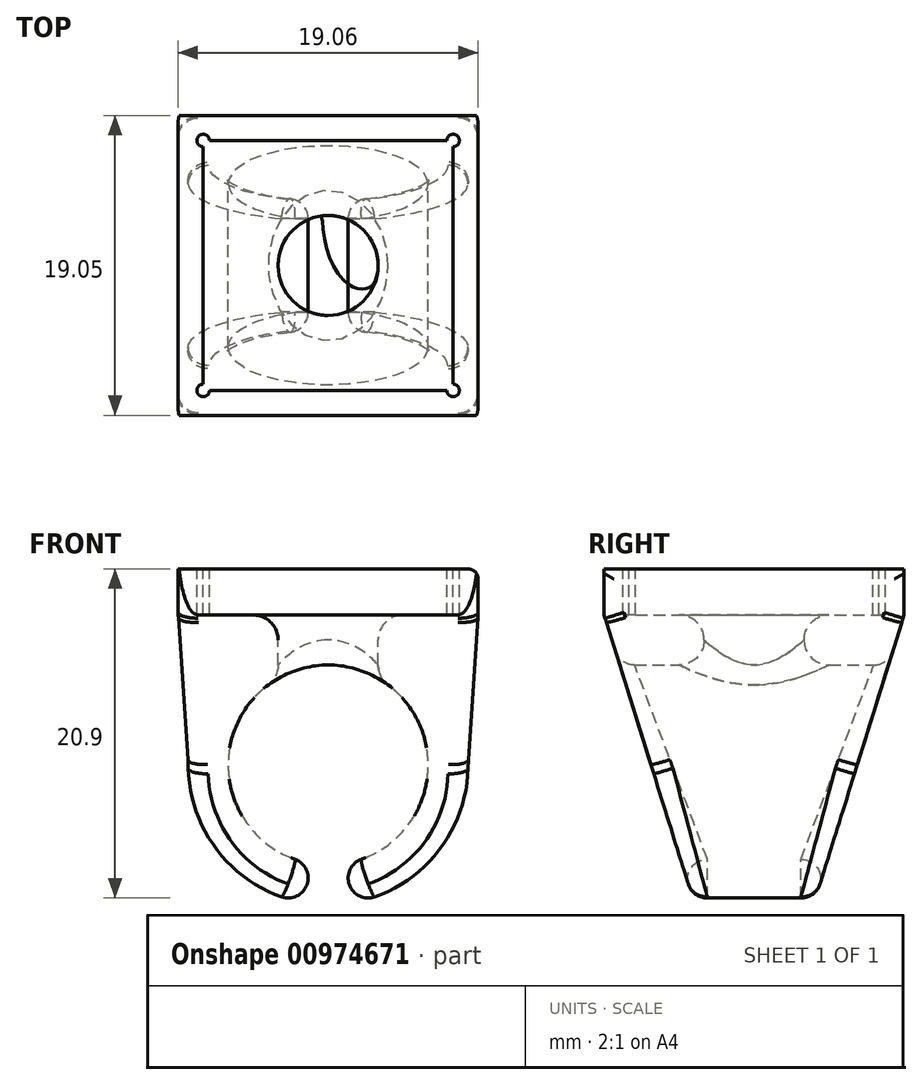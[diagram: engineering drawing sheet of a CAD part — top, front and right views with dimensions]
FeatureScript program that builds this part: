
annotation { "Feature Type Name" : "Feature", "Feature Type Description" : "" }
export const myFeature = defineFeature(function(context is Context, id is Id, definition is map)
    precondition{}
    {
        {
            var Q0;
            Q0=qCreatedBy(makeId("Front.planeOp"),FACE);
            var sketch = newSketch(context, id + "F0", { "sketchPlane" : qUnion([Q0])});
            skCircle(sketch, "E0", {"center": v(0, 0) * mm, "radius": 6.35 * mm});
            skCircle(sketch, "E1", {"center": v(0, 0) * mm, "radius": 8.9 * mm});
            skLineSegment(sketch, "E2", {"start": v(-8.9, 0) * mm, "end": v(-9.53, 9.52) * mm});
            skLineSegment(sketch, "E3", {"start": v(-9.53, 9.52) * mm, "end": v(-9.53, 12.45) * mm});
            skLineSegment(sketch, "E4", {"start": v(-9.53, 12.45) * mm, "end": v(-7.94, 12.45) * mm});
            skLineSegment(sketch, "E5", {"start": v(-7.94, 12.45) * mm, "end": v(-7.94, 9.52) * mm});
            skLineSegment(sketch, "E6", {"start": v(-7.94, 9.52) * mm, "end": v(0, 9.53) * mm});
            skLineSegment(sketch, "E7", {"start": v(0, 9.52) * mm, "end": v(0, 0) * mm});
            skLineSegment(sketch, "E8.MirrorCS", {"start": v(7.94, 9.52) * mm, "end": v(0, 9.53) * mm});
            skLineSegment(sketch, "E9.MirrorCS", {"start": v(7.94, 12.45) * mm, "end": v(7.94, 9.53) * mm});
            skLineSegment(sketch, "E10.MirrorCS", {"start": v(9.52, 12.45) * mm, "end": v(7.94, 12.45) * mm});
            skLineSegment(sketch, "E11.MirrorCS", {"start": v(9.53, 9.53) * mm, "end": v(9.53, 12.45) * mm});
            skLineSegment(sketch, "E12.MirrorCS", {"start": v(8.9, 0) * mm, "end": v(9.53, 9.52) * mm});
            skLineSegment(sketch, "E13", {"start": v(0, 0) * mm, "end": v(-1.27, 0) * mm});
            skLineSegment(sketch, "E14", {"start": v(-1.27, 0) * mm, "end": v(-1.27, -9.53) * mm});
            skLineSegment(sketch, "E15", {"start": v(-1.27, -9.53) * mm, "end": v(0, -9.53) * mm});
            skLineSegment(sketch, "E16.MirrorCS", {"start": v(0, 0) * mm, "end": v(1.27, 0) * mm});
            skLineSegment(sketch, "E17.MirrorCS", {"start": v(1.27, 0) * mm, "end": v(1.27, -9.53) * mm});
            skLineSegment(sketch, "E18.MirrorCS", {"start": v(1.27, -9.53) * mm, "end": v(0, -9.53) * mm});
            skSolve(sketch);
        }
        {
            var Q0;
            {var subQ0=sQuery(id+"F0.wireOp",EDGE,"E2");Q0=makeQuery(id+"F0.imprint","IMPRINT",FACE,{"disambiguationData":[TD([[makeQuery(id+"F0.imprint","IMPRINT",EDGE,{"derivedFrom":subQ0}),-1.0]])]});}
            var Q1;
            {var subQ0=sQuery(id+"F0.wireOp",EDGE,"E8.MirrorCS");Q1=makeQuery(id+"F0.imprint","IMPRINT",FACE,{"disambiguationData":[TD([[makeQuery(id+"F0.imprint","IMPRINT",EDGE,{"derivedFrom":subQ0}),1.0]])]});}
            var Q2;
            {var subQ1=sQuery(id+"F0.wireOp",EDGE,"E0");var subQ6=sQuery(id+"F0.wireOp",EDGE,"E14");var subQ8=makeQuery(id+"F0.imprint","INTERSECT",VERTEX,{"derivedFrom":[subQ1,subQ6]});Q2=makeQuery(id+"F0.imprint","IMPRINT",FACE,{"disambiguationData":[TD([[makeQuery(id+"F0.imprint","IMPRINT",EDGE,{"disambiguationData":[TD([[subQ8,1.0]])],"derivedFrom":subQ1}),-1.0]])]});}
            var Q3;
            {var subQ0=sQuery(id+"F0.wireOp",EDGE,"E7");var subQ1=sQuery(id+"F0.wireOp",EDGE,"E0");var subQ2=makeQuery(id+"F0.imprint","INTERSECT",VERTEX,{"derivedFrom":[subQ1,subQ0]});Q3=makeQuery(id+"F0.imprint","IMPRINT",FACE,{"disambiguationData":[TD([[makeQuery(id+"F0.imprint","IMPRINT",EDGE,{"disambiguationData":[TD([[subQ2,1.0]])],"derivedFrom":subQ1}),-1.0]])]});}
            extrude(context, id + "F1", {"entities" : qUnion([Q0, Q1, Q2, Q3]), "depth" : 19.05 * mm, "offsetDistance" : 25.4 * mm});
        }
        {
            var Q0;
            Q0=makeQuery(id+"F1.opExtrude","SWEPT_FACE",FACE,{"disambiguationData":[OSD([sQuery(id+"F0.wireOp",EDGE,"E6"),sQuery(id+"F0.wireOp",EDGE,"E8.MirrorCS")])]});
            var sketch = newSketch(context, id + "F2", { "sketchPlane" : qUnion([Q0])});
            skLineSegment(sketch, "E19.bottom", {"start": v(-7.94, 0) * mm, "end": v(7.94, 0) * mm});
            skLineSegment(sketch, "E19.top", {"start": v(-7.94, -1.59) * mm, "end": v(7.94, -1.59) * mm});
            skLineSegment(sketch, "E19.left", {"start": v(-7.94, 0) * mm, "end": v(-7.94, -1.59) * mm});
            skLineSegment(sketch, "E19.right", {"start": v(7.94, 0) * mm, "end": v(7.94, -1.59) * mm});
            skLineSegment(sketch, "E20.bottom", {"start": v(-7.94, -19.05) * mm, "end": v(7.94, -19.05) * mm});
            skLineSegment(sketch, "E20.top", {"start": v(-7.94, -17.46) * mm, "end": v(7.94, -17.46) * mm});
            skLineSegment(sketch, "E20.left", {"start": v(-7.94, -19.05) * mm, "end": v(-7.94, -17.46) * mm});
            skLineSegment(sketch, "E20.right", {"start": v(7.94, -19.05) * mm, "end": v(7.94, -17.46) * mm});
            skCircle(sketch, "E21", {"center": v(0, -9.53) * mm, "radius": 3.18 * mm});
            skPoint(sketch, "E21.centerSnap0", {"position": v(-7.94, -9.53) * mm});
            skSolve(sketch);
        }
        {
            var Q0;
            Q0=makeQuery(id+"F2.imprint","IMPRINT",FACE,{"disambiguationData":[TD([[makeQuery(id+"F2.imprint","IMPRINT",EDGE,{"derivedFrom":sQuery(id+"F2.wireOp",EDGE,"E19.bottom")}),-1.0]])]});
            var Q1;
            Q1=makeQuery(id+"F2.imprint","IMPRINT",FACE,{"disambiguationData":[TD([[makeQuery(id+"F2.imprint","IMPRINT",EDGE,{"derivedFrom":sQuery(id+"F2.wireOp",EDGE,"E20.bottom")}),1.0]])]});
            var Q2;
            Q2=makeQuery(id+"F1.opExtrude","SWEPT_FACE",FACE,{"disambiguationData":[OSD([sQuery(id+"F0.wireOp",EDGE,"E4")])]});
            extrude(context, id + "F3", {"entities" : qUnion([Q0, Q1]), "operationType" : NewBodyOperationType.ADD, "endBound" : BoundingType.UP_TO_SURFACE, "depth" : 25.4 * mm, "endBoundEntityFace" : qUnion([Q2]), "offsetDistance" : 25.4 * mm});
        }
        {
            var Q0;
            Q0=makeQuery(id+"F1.opExtrude","SWEPT_FACE",FACE,{"disambiguationData":[OSD([sQuery(id+"F0.wireOp",EDGE,"E11.MirrorCS")])]});
            var sketch = newSketch(context, id + "F4", { "sketchPlane" : qUnion([Q0])});
            skLineSegment(sketch, "E22", {"start": v(-9.53, 9.52) * mm, "end": v(-9.53, -10.8) * mm, "construction": true});
            skLineSegment(sketch, "E23", {"start": v(-9.53, -10.8) * mm, "end": v(-12.7, -10.8) * mm});
            skLineSegment(sketch, "E24", {"start": v(-12.7, -10.8) * mm, "end": v(-19.05, 9.53) * mm});
            skLineSegment(sketch, "E25.MirrorCS", {"start": v(-6.35, -10.8) * mm, "end": v(0, 9.52) * mm});
            skLineSegment(sketch, "E26.MirrorCS", {"start": v(-9.53, -10.8) * mm, "end": v(-6.35, -10.8) * mm});
            skLineSegment(sketch, "E27", {"start": v(-19.05, 9.52) * mm, "end": v(-19.05, -10.8) * mm});
            skLineSegment(sketch, "E28", {"start": v(-19.05, -10.8) * mm, "end": v(-12.7, -10.8) * mm});
            skLineSegment(sketch, "E29.MirrorCS", {"start": v(0, 9.52) * mm, "end": v(0, -10.8) * mm});
            skLineSegment(sketch, "E30.MirrorCS", {"start": v(0, -10.8) * mm, "end": v(-6.35, -10.8) * mm});
            skSolve(sketch);
        }
        {
            var Q0;
            Q0=makeQuery(id+"F4.imprint","IMPRINT",FACE,{"disambiguationData":[TD([[makeQuery(id+"F4.imprint","IMPRINT",EDGE,{"derivedFrom":sQuery(id+"F4.wireOp",EDGE,"E24")}),1.0]])]});
            var Q1;
            Q1=makeQuery(id+"F4.imprint","IMPRINT",FACE,{"disambiguationData":[TD([[makeQuery(id+"F4.imprint","IMPRINT",EDGE,{"derivedFrom":sQuery(id+"F4.wireOp",EDGE,"E25.MirrorCS")}),-1.0]])]});
            extrude(context, id + "F5", {"entities" : qUnion([Q0, Q1]), "operationType" : NewBodyOperationType.REMOVE, "endBound" : BoundingType.THROUGH_ALL, "oppositeDirection" : true, "depth" : 25.4 * mm, "offsetDistance" : 25.4 * mm});
        }
        {
            var Q0;
            Q0=makeQuery(id+"F1.opExtrude","SWEPT_EDGE",EDGE,{"disambiguationData":[OSD([sQuery(id+"F0.wireOp",EDGE,"E0"),sQuery(id+"F0.wireOp",EDGE,"E14")])]});
            var Q1;
            Q1=makeQuery(id+"F1.opExtrude","SWEPT_EDGE",EDGE,{"disambiguationData":[OSD([sQuery(id+"F0.wireOp",EDGE,"E1"),sQuery(id+"F0.wireOp",EDGE,"E14")])]});
            var Q2;
            Q2=makeQuery(id+"F1.opExtrude","SWEPT_EDGE",EDGE,{"disambiguationData":[OSD([sQuery(id+"F0.wireOp",EDGE,"E0"),sQuery(id+"F0.wireOp",EDGE,"E17.MirrorCS")])]});
            var Q3;
            Q3=makeQuery(id+"F1.opExtrude","SWEPT_EDGE",EDGE,{"disambiguationData":[OSD([sQuery(id+"F0.wireOp",EDGE,"E1"),sQuery(id+"F0.wireOp",EDGE,"E17.MirrorCS")])]});
            fillet(context, id + "F6", {"entities" : qUnion([Q0, Q1, Q2, Q3]), "radius" : 1.27 * mm, "tangentPropagation" : true, "allowEdgeOverflow" : false});
        }
        {
            var Q0;
            Q0=makeQuery(id+"F1.opExtrude","SWEPT_EDGE",EDGE,{"disambiguationData":[OSD([sQuery(id+"F0.wireOp",EDGE,"E1"),sQuery(id+"F0.wireOp",EDGE,"E12.MirrorCS")])]});
            var Q1;
            Q1=makeQuery(id+"F1.opExtrude","SWEPT_EDGE",EDGE,{"disambiguationData":[OSD([sQuery(id+"F0.wireOp",EDGE,"E1"),sQuery(id+"F0.wireOp",EDGE,"E2")])]});
            fillet(context, id + "F7", {"entities" : qUnion([Q0, Q1]), "radius" : 12.7 * mm, "tangentPropagation" : true, "allowEdgeOverflow" : false});
        }
        {
            var Q0;
            Q0=makeQuery(id+"F2.imprint","IMPRINT",FACE,{"disambiguationData":[TD([[makeQuery(id+"F2.imprint","IMPRINT",EDGE,{"derivedFrom":sQuery(id+"F2.wireOp",EDGE,"E21")}),1.0]])]});
            extrude(context, id + "F8", {"entities" : qUnion([Q0]), "operationType" : NewBodyOperationType.REMOVE, "endBound" : BoundingType.UP_TO_NEXT, "oppositeDirection" : true, "depth" : 25.4 * mm, "offsetDistance" : 25.4 * mm});
        }
        {
            var Q0;
            Q0=makeQuery(id+"F8.boolean.opBoolean","COPY",FACE,{"derivedFrom":makeQuery(id+"F8.opExtrude","SWEPT_FACE",FACE,{"disambiguationData":[OSD([sQuery(id+"F2.wireOp",EDGE,"E21")])]})});
            fillet(context, id + "F9", {"entities" : qUnion([Q0]), "radius" : 1.59 * mm, "tangentPropagation" : true, "allowEdgeOverflow" : false});
        }
        {
            var Q0;
            Q0=makeQuery(id+"F3.boolean.opBoolean","MERGE",FACE,{"derivedFrom":[makeQuery(id+"F1.opExtrude","SWEPT_FACE",FACE,{"disambiguationData":[OSD([sQuery(id+"F0.wireOp",EDGE,"E4")])]}),makeQuery(id+"F1.opExtrude","SWEPT_FACE",FACE,{"disambiguationData":[OSD([sQuery(id+"F0.wireOp",EDGE,"E10.MirrorCS")])]}),makeQuery(id+"F3.opExtrude","CAP_FACE",FACE,{"disambiguationData":[OSD([sQuery(id+"F2.wireOp",EDGE,"E19.bottom"),sQuery(id+"F2.wireOp",EDGE,"E19.top"),sQuery(id+"F2.wireOp",EDGE,"E19.left"),sQuery(id+"F2.wireOp",EDGE,"E19.right")])],"isStart":false}),makeQuery(id+"F3.opExtrude","CAP_FACE",FACE,{"disambiguationData":[OSD([sQuery(id+"F2.wireOp",EDGE,"E20.bottom"),sQuery(id+"F2.wireOp",EDGE,"E20.top"),sQuery(id+"F2.wireOp",EDGE,"E20.left"),sQuery(id+"F2.wireOp",EDGE,"E20.right")])],"isStart":false})]});
            var sketch = newSketch(context, id + "F10", { "sketchPlane" : qUnion([Q0])});
            skCircle(sketch, "E31", {"center": v(-7.94, -1.59) * mm, "radius": 0.4 * mm});
            skCircle(sketch, "E32", {"center": v(-7.94, -17.46) * mm, "radius": 0.4 * mm});
            skCircle(sketch, "E33", {"center": v(7.94, -17.46) * mm, "radius": 0.4 * mm});
            skCircle(sketch, "E34", {"center": v(7.94, -1.59) * mm, "radius": 0.4 * mm});
            skSolve(sketch);
        }
        {
            var Q0;
            {var subQ0=sQuery(id+"F10.wireOp",EDGE,"E31");var subQ1=makeQuery(id+"F3.opExtrude","CAP_EDGE",EDGE,{"disambiguationData":[OSD([sQuery(id+"F2.wireOp",EDGE,"E19.top")])],"isStart":false});var subQ2=makeQuery(id+"F10.imprint","INTERSECT",VERTEX,{"derivedFrom":[subQ1,subQ0]});Q0=makeQuery(id+"F10.imprint","IMPRINT",FACE,{"disambiguationData":[TD([[makeQuery(id+"F10.imprint","IMPRINT",EDGE,{"disambiguationData":[TD([[subQ2,-1.0]])],"derivedFrom":subQ0}),1.0]])]});}
            var Q1;
            {var subQ0=sQuery(id+"F10.wireOp",EDGE,"E32");var subQ1=makeQuery(id+"F3.opExtrude","CAP_EDGE",EDGE,{"disambiguationData":[OSD([sQuery(id+"F2.wireOp",EDGE,"E20.top")])],"isStart":false});var subQ2=makeQuery(id+"F10.imprint","INTERSECT",VERTEX,{"derivedFrom":[subQ1,subQ0]});Q1=makeQuery(id+"F10.imprint","IMPRINT",FACE,{"disambiguationData":[TD([[makeQuery(id+"F10.imprint","IMPRINT",EDGE,{"disambiguationData":[TD([[subQ2,1.0]])],"derivedFrom":subQ0}),1.0]])]});}
            var Q2;
            {var subQ0=sQuery(id+"F10.wireOp",EDGE,"E33");var subQ1=makeQuery(id+"F3.opExtrude","CAP_EDGE",EDGE,{"disambiguationData":[OSD([sQuery(id+"F2.wireOp",EDGE,"E20.top")])],"isStart":false});var subQ2=makeQuery(id+"F10.imprint","INTERSECT",VERTEX,{"derivedFrom":[subQ1,subQ0]});Q2=makeQuery(id+"F10.imprint","IMPRINT",FACE,{"disambiguationData":[TD([[makeQuery(id+"F10.imprint","IMPRINT",EDGE,{"disambiguationData":[TD([[subQ2,-1.0]])],"derivedFrom":subQ0}),1.0]])]});}
            var Q3;
            {var subQ0=sQuery(id+"F10.wireOp",EDGE,"E34");var subQ1=makeQuery(id+"F3.opExtrude","CAP_EDGE",EDGE,{"disambiguationData":[OSD([sQuery(id+"F2.wireOp",EDGE,"E19.top")])],"isStart":false});var subQ2=makeQuery(id+"F10.imprint","INTERSECT",VERTEX,{"derivedFrom":[subQ1,subQ0]});Q3=makeQuery(id+"F10.imprint","IMPRINT",FACE,{"disambiguationData":[TD([[makeQuery(id+"F10.imprint","IMPRINT",EDGE,{"disambiguationData":[TD([[subQ2,1.0]])],"derivedFrom":subQ0}),1.0]])]});}
            var Q4;
            Q4=makeQuery(id+"F1.opExtrude","SWEPT_FACE",FACE,{"disambiguationData":[OSD([sQuery(id+"F0.wireOp",EDGE,"E6"),sQuery(id+"F0.wireOp",EDGE,"E8.MirrorCS")])]});
            extrude(context, id + "F11", {"entities" : qUnion([Q0, Q1, Q2, Q3]), "operationType" : NewBodyOperationType.REMOVE, "endBound" : BoundingType.UP_TO_SURFACE, "oppositeDirection" : true, "depth" : 25.4 * mm, "endBoundEntityFace" : qUnion([Q4]), "offsetDistance" : 25.4 * mm});
        }
        {
            var Q0;
            Q0=makeQuery(id+"F1.opExtrude","SWEPT_EDGE",EDGE,{"disambiguationData":[OSD([sQuery(id+"F0.wireOp",EDGE,"E11.MirrorCS"),sQuery(id+"F0.wireOp",EDGE,"E12.MirrorCS")])]});
            var Q1;
            Q1=makeQuery(id+"F5.boolean.opBoolean","COPY",EDGE,{"derivedFrom":makeQuery(id+"F5.opExtrude","SWEPT_EDGE",EDGE,{"disambiguationData":[OSD([sQuery(id+"F0.wireOp",EDGE,"E11.MirrorCS"),sQuery(id+"F0.wireOp",EDGE,"E12.MirrorCS"),sQuery(id+"F4.wireOp",EDGE,"E24"),sQuery(id+"F4.wireOp",EDGE,"E27")])]})});
            var Q2;
            Q2=makeQuery(id+"F5.boolean.opBoolean","COPY",EDGE,{"derivedFrom":makeQuery(id+"F5.opExtrude","SWEPT_EDGE",EDGE,{"disambiguationData":[OSD([sQuery(id+"F0.wireOp",EDGE,"E11.MirrorCS"),sQuery(id+"F0.wireOp",EDGE,"E12.MirrorCS"),sQuery(id+"F4.wireOp",EDGE,"E25.MirrorCS"),sQuery(id+"F4.wireOp",EDGE,"E29.MirrorCS")])]})});
            var Q3;
            Q3=makeQuery(id+"F1.opExtrude","SWEPT_EDGE",EDGE,{"disambiguationData":[OSD([sQuery(id+"F0.wireOp",EDGE,"E2"),sQuery(id+"F0.wireOp",EDGE,"E3")])]});
            fillet(context, id + "F12", {"entities" : qUnion([Q0, Q1, Q2, Q3]), "radius" : 5.08 * mm, "tangentPropagation" : true, "allowEdgeOverflow" : false});
        }
        {
            var Q0;
            Q0=makeQuery(id+"F1.opExtrude","SWEPT_EDGE",EDGE,{"disambiguationData":[OSD([sQuery(id+"F0.wireOp",EDGE,"E10.MirrorCS"),sQuery(id+"F0.wireOp",EDGE,"E11.MirrorCS")])]});
            fillet(context, id + "F13", {"entities" : qUnion([Q0]), "radius" : 0.64 * mm, "tangentPropagation" : true, "allowEdgeOverflow" : false});
        }
        {
            var Q0;
            {var subQ0=sQuery(id+"F0.wireOp",EDGE,"E1");Q0=makeQuery(id+"F5.boolean.opBoolean","INTERSECT",EDGE,{"derivedFrom":[makeQuery(id+"F1.opExtrude","SWEPT_FACE",FACE,{"disambiguationData":[OSD([subQ0]),TDD([makeQuery(id+"F0.imprint","IMPRINT",EDGE,{"disambiguationData":[TD([[makeQuery(id+"F0.imprint","INTERSECT",VERTEX,{"derivedFrom":[subQ0,sQuery(id+"F0.wireOp",EDGE,"E12.MirrorCS")]}),1.0]])],"derivedFrom":subQ0})])]}),makeQuery(id+"F5.opExtrude","SWEPT_FACE",FACE,{"disambiguationData":[OSD([sQuery(id+"F4.wireOp",EDGE,"E24")])]})]});}
            var Q1;
            {var subQ0=sQuery(id+"F0.wireOp",EDGE,"E1");Q1=makeQuery(id+"F5.boolean.opBoolean","INTERSECT",EDGE,{"derivedFrom":[makeQuery(id+"F1.opExtrude","SWEPT_FACE",FACE,{"disambiguationData":[OSD([subQ0]),TDD([makeQuery(id+"F0.imprint","IMPRINT",EDGE,{"disambiguationData":[TD([[makeQuery(id+"F0.imprint","INTERSECT",VERTEX,{"derivedFrom":[subQ0,sQuery(id+"F0.wireOp",EDGE,"E12.MirrorCS")]}),1.0]])],"derivedFrom":subQ0})])]}),makeQuery(id+"F5.opExtrude","SWEPT_FACE",FACE,{"disambiguationData":[OSD([sQuery(id+"F4.wireOp",EDGE,"E25.MirrorCS")])]})]});}
            fillet(context, id + "F14", {"entities" : qUnion([Q0, Q1]), "radius" : 1.27 * mm, "tangentPropagation" : true, "allowEdgeOverflow" : false});
        }
    });
